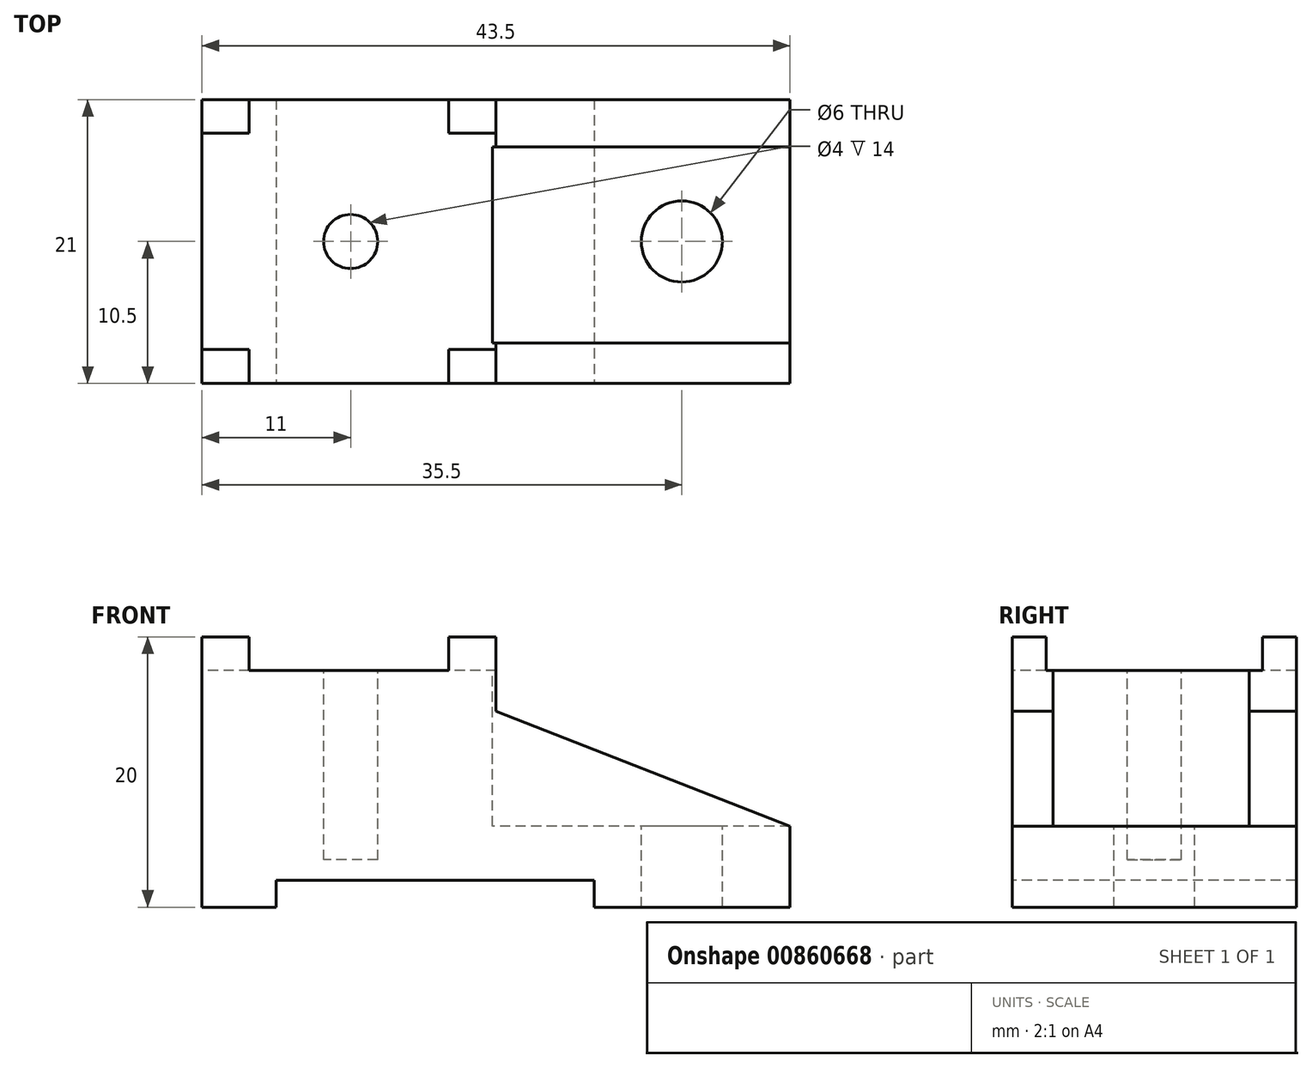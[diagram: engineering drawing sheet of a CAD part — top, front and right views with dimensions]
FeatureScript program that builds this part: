
annotation { "Feature Type Name" : "Feature", "Feature Type Description" : "" }
export const myFeature = defineFeature(function(context is Context, id is Id, definition is map)
    precondition{}
    {
        {
            var Q0;
            Q0=qCreatedBy(makeId("Front.planeOp"),FACE);
            var sketch = newSketch(context, id + "F0", { "sketchPlane" : qUnion([Q0])});
            skLineSegment(sketch, "E0.bottom", {"start": v(0, 0) * mm, "end": v(43.5, 0) * mm});
            skLineSegment(sketch, "E0.top", {"start": v(0, 20) * mm, "end": v(43.5, 20) * mm});
            skLineSegment(sketch, "E0.left", {"start": v(0, 0) * mm, "end": v(0, 20) * mm});
            skLineSegment(sketch, "E0.right", {"start": v(43.5, 0) * mm, "end": v(43.5, 20) * mm});
            skSolve(sketch);
        }
        {
            var Q0;
            Q0=makeQuery(id+"F0.imprint","IMPRINT",FACE,{"disambiguationData":[TD([[makeQuery(id+"F0.imprint","IMPRINT",EDGE,{"derivedFrom":sQuery(id+"F0.wireOp",EDGE,"E0.bottom")}),1.0]])]});
            extrude(context, id + "F1", {"entities" : qUnion([Q0]), "depth" : 21 * mm, "offsetDistance" : 25 * mm});
        }
        {
            var Q0;
            Q0=makeQuery(id+"F1.opExtrude","SWEPT_FACE",FACE,{"disambiguationData":[OSD([sQuery(id+"F0.wireOp",EDGE,"E0.top")])]});
            var sketch = newSketch(context, id + "F2", { "sketchPlane" : qUnion([Q0])});
            skCircle(sketch, "E1", {"center": v(35.5, -10.5) * mm, "radius": 3 * mm});
            skCircle(sketch, "E2", {"center": v(11, -10.5) * mm, "radius": 2 * mm});
            skSolve(sketch);
        }
        {
            var Q0;
            Q0=makeQuery(id+"F2.imprint","IMPRINT",FACE,{"disambiguationData":[TD([[makeQuery(id+"F2.imprint","IMPRINT",EDGE,{"derivedFrom":sQuery(id+"F2.wireOp",EDGE,"E1")}),-1.0]])]});
            var sketch = newSketch(context, id + "F3", { "sketchPlane" : qUnion([Q0])});
            skLineSegment(sketch, "E3.bottom", {"start": v(43.48, -3.5) * mm, "end": v(21.48, -3.5) * mm});
            skLineSegment(sketch, "E3.top", {"start": v(43.48, -17.5) * mm, "end": v(21.48, -17.5) * mm});
            skLineSegment(sketch, "E3.left", {"start": v(43.48, -3.5) * mm, "end": v(43.48, -17.5) * mm});
            skLineSegment(sketch, "E3.right", {"start": v(21.48, -3.5) * mm, "end": v(21.48, -17.5) * mm});
            skPoint(sketch, "E3.middle", {"position": v(32.48, -10.5) * mm});
            skSolve(sketch);
        }
        {
            var Q0;
            Q0=makeQuery(id+"F3.imprint","IMPRINT",FACE,{"disambiguationData":[TD([[makeQuery(id+"F3.imprint","IMPRINT",EDGE,{"derivedFrom":makeQuery(id+"F2.imprint","IMPRINT",EDGE,{"derivedFrom":sQuery(id+"F2.wireOp",EDGE,"E1")})}),1.0]])]});
            extrude(context, id + "F4", {"entities" : qUnion([Q0]), "operationType" : NewBodyOperationType.REMOVE, "endBound" : BoundingType.THROUGH_ALL, "oppositeDirection" : true, "depth" : 25 * mm, "offsetDistance" : 25 * mm});
        }
        {
            var Q0;
            Q0=makeQuery(id+"F2.imprint","IMPRINT",FACE,{"disambiguationData":[TD([[makeQuery(id+"F2.imprint","IMPRINT",EDGE,{"derivedFrom":sQuery(id+"F2.wireOp",EDGE,"E2")}),1.0]])]});
            extrude(context, id + "F5", {"entities" : qUnion([Q0]), "operationType" : NewBodyOperationType.REMOVE, "oppositeDirection" : true, "depth" : 16.5 * mm, "offsetDistance" : 25 * mm});
        }
        {
            var Q0;
            Q0=makeQuery(id+"F1.opExtrude","SWEPT_FACE",FACE,{"disambiguationData":[OSD([sQuery(id+"F0.wireOp",EDGE,"E0.top")])]});
            var sketch = newSketch(context, id + "F6", { "sketchPlane" : qUnion([Q0])});
            skLineSegment(sketch, "E4.bottom", {"start": v(43.5, -18) * mm, "end": v(21.5, -18) * mm});
            skLineSegment(sketch, "E4.top", {"start": v(43.5, -3.5) * mm, "end": v(21.5, -3.5) * mm});
            skLineSegment(sketch, "E4.left", {"start": v(43.5, -18) * mm, "end": v(43.5, -3.5) * mm});
            skLineSegment(sketch, "E4.right", {"start": v(21.5, -18) * mm, "end": v(21.5, -3.5) * mm});
            skPoint(sketch, "E4.middle", {"position": v(32.5, -10.75) * mm});
            skSolve(sketch);
        }
        {
            var Q0;
            Q0=makeQuery(id+"F6.imprint","IMPRINT",FACE,{"disambiguationData":[TD([[makeQuery(id+"F6.imprint","IMPRINT",EDGE,{"derivedFrom":sQuery(id+"F6.wireOp",EDGE,"E4.bottom")}),-1.0]])]});
            extrude(context, id + "F7", {"entities" : qUnion([Q0]), "operationType" : NewBodyOperationType.REMOVE, "oppositeDirection" : true, "depth" : 14 * mm, "offsetDistance" : 25 * mm});
        }
        {
            var Q0;
            Q0=makeQuery(id+"F1.opExtrude","CAP_FACE",FACE,{"disambiguationData":[OSD([sQuery(id+"F0.wireOp",EDGE,"E0.bottom"),sQuery(id+"F0.wireOp",EDGE,"E0.top"),sQuery(id+"F0.wireOp",EDGE,"E0.left"),sQuery(id+"F0.wireOp",EDGE,"E0.right")])],"isStart":false});
            var sketch = newSketch(context, id + "F8", { "sketchPlane" : qUnion([Q0])});
            skLineSegment(sketch, "E5", {"start": v(21.75, 20) * mm, "end": v(21.75, 14.5) * mm});
            skLineSegment(sketch, "E6", {"start": v(21.75, 14.5) * mm, "end": v(43.5, 6) * mm});
            skSolve(sketch);
        }
        {
            var Q0;
            {var subQ0=sQuery(id+"F8.wireOp",EDGE,"E5");Q0=makeQuery(id+"F8.imprint","IMPRINT",FACE,{"disambiguationData":[TD([[makeQuery(id+"F8.imprint","IMPRINT",EDGE,{"derivedFrom":subQ0}),1.0]])]});}
            var sketch = newSketch(context, id + "F9", { "sketchPlane" : qUnion([Q0])});
            skSolve(sketch);
        }
        {
            var Q0;
            {var subQ0=sQuery(id+"F8.wireOp",EDGE,"E5");Q0=makeQuery(id+"F8.imprint","IMPRINT",FACE,{"disambiguationData":[TD([[makeQuery(id+"F8.imprint","IMPRINT",EDGE,{"derivedFrom":subQ0}),1.0]])]});}
            var sketch = newSketch(context, id + "F10", { "sketchPlane" : qUnion([Q0])});
            skSolve(sketch);
        }
        {
            var Q0;
            Q0 = qSketchRegion(id + "F9", true);
            var Q1;
            {var subQ0=sQuery(id+"F8.wireOp",EDGE,"E5");Q1=makeQuery(id+"F10.imprint","IMPRINT",FACE,{"disambiguationData":[TD([[makeQuery(id+"F10.imprint","IMPRINT",EDGE,{"derivedFrom":makeQuery(id+"F8.imprint","IMPRINT",EDGE,{"derivedFrom":subQ0})}),1.0]])]});}
            extrude(context, id + "F11", {"entities" : qUnion([Q0, Q1]), "operationType" : NewBodyOperationType.REMOVE, "endBound" : BoundingType.THROUGH_ALL, "oppositeDirection" : true, "depth" : 25 * mm, "offsetDistance" : 25 * mm});
        }
        {
            var Q0;
            {var subQ3=sQuery(id+"F8.wireOp",EDGE,"E5");Q0=makeQuery(id+"F8.imprint","IMPRINT",FACE,{"disambiguationData":[TD([[makeQuery(id+"F8.imprint","IMPRINT",EDGE,{"derivedFrom":subQ3}),-1.0]])]});}
            var sketch = newSketch(context, id + "F12", { "sketchPlane" : qUnion([Q0])});
            skLineSegment(sketch, "E7.bottom", {"start": v(5.5, 0) * mm, "end": v(29, 0) * mm});
            skLineSegment(sketch, "E7.top", {"start": v(5.5, 2) * mm, "end": v(29, 2) * mm});
            skLineSegment(sketch, "E7.left", {"start": v(5.5, 0) * mm, "end": v(5.5, 2) * mm});
            skLineSegment(sketch, "E7.right", {"start": v(29, 0) * mm, "end": v(29, 2) * mm});
            skLineSegment(sketch, "E8.bottom", {"start": v(3.5, 20) * mm, "end": v(18.25, 20) * mm});
            skLineSegment(sketch, "E8.top", {"start": v(3.5, 17.5) * mm, "end": v(18.25, 17.5) * mm});
            skLineSegment(sketch, "E8.left", {"start": v(3.5, 20) * mm, "end": v(3.5, 17.5) * mm});
            skLineSegment(sketch, "E8.right", {"start": v(18.25, 20) * mm, "end": v(18.25, 17.5) * mm});
            skLineSegment(sketch, "E9.bottom", {"start": v(6, 17.5) * mm, "end": v(15.75, 17.5) * mm});
            skLineSegment(sketch, "E9.top", {"start": v(6, 14.5) * mm, "end": v(15.75, 14.5) * mm});
            skLineSegment(sketch, "E9.left", {"start": v(6, 17.5) * mm, "end": v(6, 14.5) * mm});
            skLineSegment(sketch, "E9.right", {"start": v(15.75, 17.5) * mm, "end": v(15.75, 14.5) * mm});
            skSolve(sketch);
        }
        {
            var Q0;
            Q0=makeQuery(id+"F12.imprint","IMPRINT",FACE,{"disambiguationData":[TD([[makeQuery(id+"F12.imprint","IMPRINT",EDGE,{"derivedFrom":sQuery(id+"F12.wireOp",EDGE,"E9.bottom")}),-1.0]])]});
            var Q1;
            Q1=makeQuery(id+"F12.imprint","IMPRINT",FACE,{"disambiguationData":[TD([[makeQuery(id+"F12.imprint","IMPRINT",EDGE,{"derivedFrom":sQuery(id+"F12.wireOp",EDGE,"E8.bottom")}),-1.0]])]});
            var Q2;
            Q2=makeQuery(id+"F12.imprint","IMPRINT",FACE,{"disambiguationData":[TD([[makeQuery(id+"F12.imprint","IMPRINT",EDGE,{"derivedFrom":sQuery(id+"F12.wireOp",EDGE,"E7.bottom")}),1.0]])]});
            extrude(context, id + "F13", {"entities" : qUnion([Q0, Q1, Q2]), "operationType" : NewBodyOperationType.REMOVE, "endBound" : BoundingType.THROUGH_ALL, "oppositeDirection" : true, "depth" : 25 * mm, "offsetDistance" : 25 * mm});
        }
        {
            var Q0;
            Q0=makeQuery(id+"F1.opExtrude","SWEPT_FACE",FACE,{"disambiguationData":[OSD([sQuery(id+"F0.wireOp",EDGE,"E0.left")])]});
            var sketch = newSketch(context, id + "F14", { "sketchPlane" : qUnion([Q0])});
            skLineSegment(sketch, "E10.bottom", {"start": v(2.5, 20) * mm, "end": v(18.5, 20) * mm});
            skLineSegment(sketch, "E10.top", {"start": v(2.5, 17.5) * mm, "end": v(18.5, 17.5) * mm});
            skLineSegment(sketch, "E10.left", {"start": v(2.5, 20) * mm, "end": v(2.5, 17.5) * mm});
            skLineSegment(sketch, "E10.right", {"start": v(18.5, 20) * mm, "end": v(18.5, 17.5) * mm});
            skLineSegment(sketch, "E11.bottom", {"start": v(5, 17.5) * mm, "end": v(16, 17.5) * mm});
            skLineSegment(sketch, "E11.top", {"start": v(5, 14.5) * mm, "end": v(16, 14.5) * mm});
            skLineSegment(sketch, "E11.left", {"start": v(5, 17.5) * mm, "end": v(5, 14.5) * mm});
            skLineSegment(sketch, "E11.right", {"start": v(16, 17.5) * mm, "end": v(16, 14.5) * mm});
            skSolve(sketch);
        }
        {
            var Q0;
            Q0=makeQuery(id+"F14.imprint","IMPRINT",FACE,{"disambiguationData":[TD([[makeQuery(id+"F14.imprint","IMPRINT",EDGE,{"derivedFrom":sQuery(id+"F14.wireOp",EDGE,"E10.bottom")}),1.0]])]});
            var Q1;
            Q1=makeQuery(id+"F14.imprint","IMPRINT",FACE,{"disambiguationData":[TD([[makeQuery(id+"F14.imprint","IMPRINT",EDGE,{"derivedFrom":sQuery(id+"F14.wireOp",EDGE,"E11.bottom")}),-1.0]])]});
            extrude(context, id + "F15", {"entities" : qUnion([Q0, Q1]), "operationType" : NewBodyOperationType.REMOVE, "endBound" : BoundingType.THROUGH_ALL, "oppositeDirection" : true, "depth" : 25 * mm, "offsetDistance" : 25 * mm});
        }
    });
